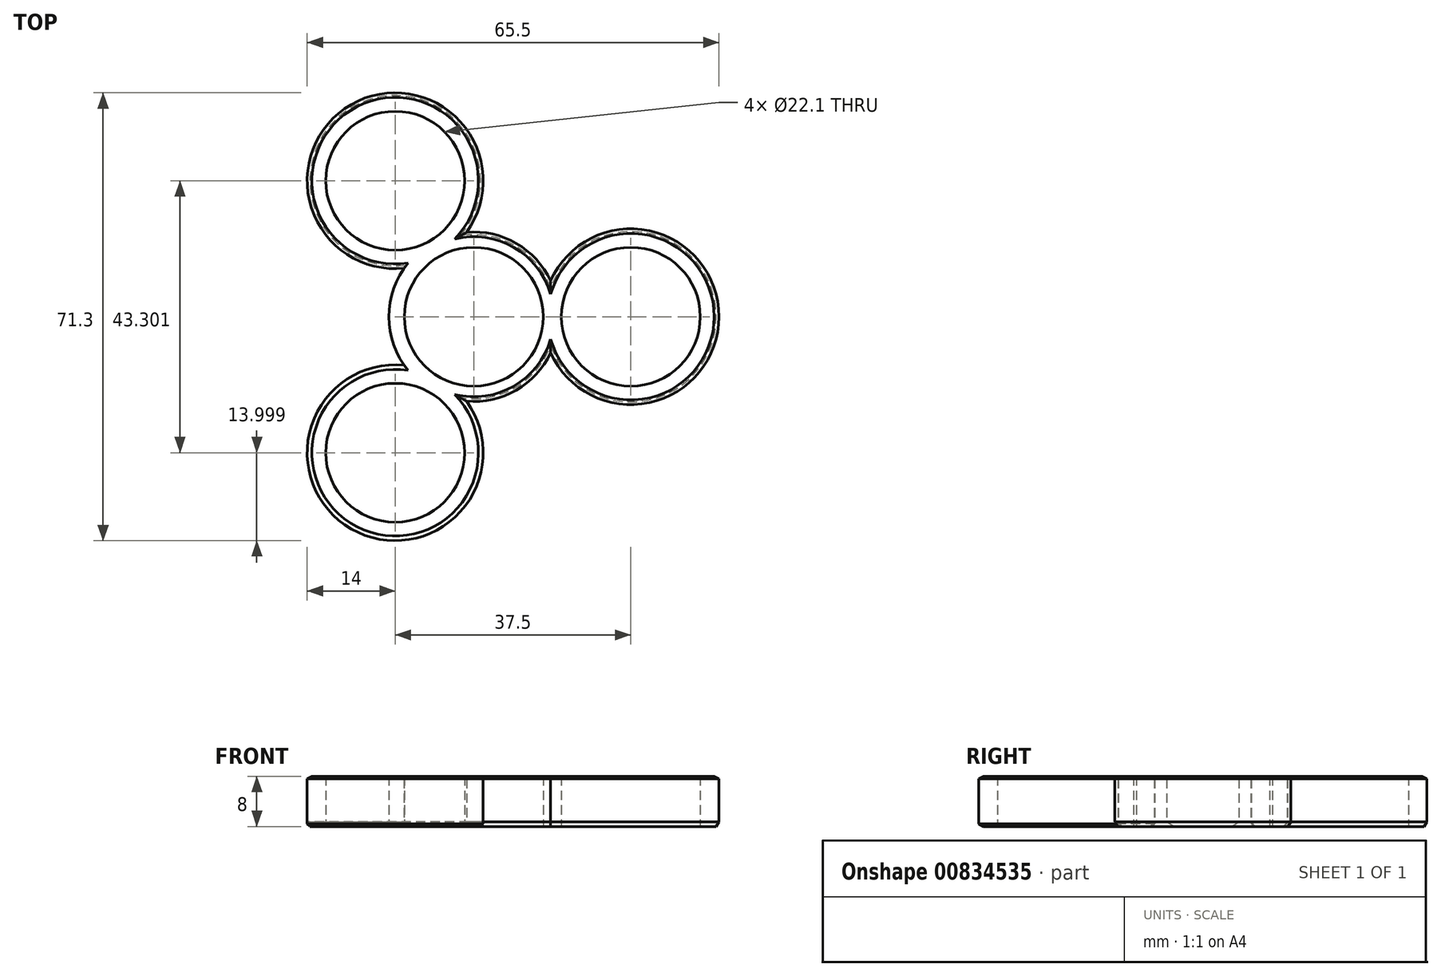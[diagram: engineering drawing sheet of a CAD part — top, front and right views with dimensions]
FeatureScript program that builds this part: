
annotation { "Feature Type Name" : "Feature", "Feature Type Description" : "" }
export const myFeature = defineFeature(function(context is Context, id is Id, definition is map)
    precondition{}
    {
        {
            var Q0;
            Q0=qCreatedBy(makeId("Top.planeOp"),FACE);
            var sketch = newSketch(context, id + "F0", { "sketchPlane" : qUnion([Q0])});
            skCircle(sketch, "E0", {"center": v(0, 0) * mm, "radius": 11.05 * mm});
            skCircle(sketch, "E1", {"center": v(25, 0) * mm, "radius": 11.05 * mm});
            skCircle(sketch, "E2.1.0", {"center": v(-12.5, 21.65) * mm, "radius": 11.05 * mm});
            skCircle(sketch, "E2.2.0", {"center": v(-12.5, -21.65) * mm, "radius": 11.05 * mm});
            skSolve(sketch);
        }
        {
            var Q0;
            Q0=qCreatedBy(makeId("Top.planeOp"),FACE);
            var sketch = newSketch(context, id + "F1", { "sketchPlane" : qUnion([Q0])});
            skPoint(sketch, "E3.0", {"position": v(-12.5, 21.65) * mm});
            skCircle(sketch, "E4.0.0", {"center": v(-12.5, 21.65) * mm, "radius": 11.05 * mm});
            skCircle(sketch, "E5.0.0", {"center": v(25, 0) * mm, "radius": 11.05 * mm});
            skCircle(sketch, "E6.0.0", {"center": v(-12.5, -21.65) * mm, "radius": 11.05 * mm});
            skCircle(sketch, "E7.0.0", {"center": v(0, 0) * mm, "radius": 11.05 * mm});
            skCircle(sketch, "E8", {"center": v(25, 0) * mm, "radius": 14 * mm});
            skCircle(sketch, "E9", {"center": v(-12.5, 21.65) * mm, "radius": 14 * mm});
            skCircle(sketch, "E10", {"center": v(-12.5, -21.65) * mm, "radius": 14 * mm});
            skCircle(sketch, "E11", {"center": v(0, 0) * mm, "radius": 13.5 * mm});
            skSolve(sketch);
        }
        {
            var Q0;
            Q0=makeQuery(id+"F1.imprint","IMPRINT",FACE,{"disambiguationData":[TD([[makeQuery(id+"F1.imprint","IMPRINT",EDGE,{"derivedFrom":sQuery(id+"F1.wireOp",EDGE,"E4.0.0")}),-1.0]])]});
            var Q1;
            Q1=makeQuery(id+"F1.imprint","IMPRINT",FACE,{"disambiguationData":[TD([[makeQuery(id+"F1.imprint","IMPRINT",EDGE,{"derivedFrom":sQuery(id+"F1.wireOp",EDGE,"E7.0.0")}),-1.0]])]});
            var Q2;
            {var subQ0=sQuery(id+"F1.wireOp",EDGE,"E11");var subQ1=sQuery(id+"F1.wireOp",EDGE,"E9");var subQ2=makeQuery(id+"F1.imprint","INTERSECT",VERTEX,{"disambiguationData":[OD(0.0)],"derivedFrom":[subQ1,subQ0]});Q2=makeQuery(id+"F1.imprint","IMPRINT",FACE,{"disambiguationData":[TD([[makeQuery(id+"F1.imprint","IMPRINT",EDGE,{"disambiguationData":[TD([[subQ2,1.0]])],"derivedFrom":subQ1}),1.0]])]});}
            var Q3;
            {var subQ0=sQuery(id+"F1.wireOp",EDGE,"E11");var subQ1=sQuery(id+"F1.wireOp",EDGE,"E8");var subQ2=makeQuery(id+"F1.imprint","INTERSECT",VERTEX,{"disambiguationData":[OD(0.0)],"derivedFrom":[subQ1,subQ0]});Q3=makeQuery(id+"F1.imprint","IMPRINT",FACE,{"disambiguationData":[TD([[makeQuery(id+"F1.imprint","IMPRINT",EDGE,{"disambiguationData":[TD([[subQ2,-1.0]])],"derivedFrom":subQ1}),1.0]])]});}
            var Q4;
            Q4=makeQuery(id+"F1.imprint","IMPRINT",FACE,{"disambiguationData":[TD([[makeQuery(id+"F1.imprint","IMPRINT",EDGE,{"derivedFrom":sQuery(id+"F1.wireOp",EDGE,"E5.0.0")}),-1.0]])]});
            var Q5;
            {var subQ0=sQuery(id+"F1.wireOp",EDGE,"E11");var subQ1=sQuery(id+"F1.wireOp",EDGE,"E10");var subQ2=makeQuery(id+"F1.imprint","INTERSECT",VERTEX,{"disambiguationData":[OD(0.0)],"derivedFrom":[subQ1,subQ0]});Q5=makeQuery(id+"F1.imprint","IMPRINT",FACE,{"disambiguationData":[TD([[makeQuery(id+"F1.imprint","IMPRINT",EDGE,{"disambiguationData":[TD([[subQ2,1.0]])],"derivedFrom":subQ1}),1.0]])]});}
            var Q6;
            Q6=makeQuery(id+"F1.imprint","IMPRINT",FACE,{"disambiguationData":[TD([[makeQuery(id+"F1.imprint","IMPRINT",EDGE,{"derivedFrom":sQuery(id+"F1.wireOp",EDGE,"E6.0.0")}),-1.0]])]});
            extrude(context, id + "F2", {"entities" : qUnion([Q0, Q1, Q2, Q3, Q4, Q5, Q6]), "depth" : 8 * mm, "offsetDistance" : 25 * mm});
        }
        {
            var Q0;
            Q0=makeQuery(id+"F2.opExtrude","CAP_EDGE",EDGE,{"disambiguationData":[OSD([sQuery(id+"F1.wireOp",EDGE,"E10")])],"isStart":false});
            var Q1;
            {var subQ0=sQuery(id+"F1.wireOp",EDGE,"E11");Q1=makeQuery(id+"F2.opExtrude","CAP_EDGE",EDGE,{"disambiguationData":[OSD([subQ0]),TDD([makeQuery(id+"F1.imprint","IMPRINT",EDGE,{"disambiguationData":[TD([[makeQuery(id+"F1.imprint","INTERSECT",VERTEX,{"disambiguationData":[OD(1.0)],"derivedFrom":[sQuery(id+"F1.wireOp",EDGE,"E8"),subQ0]}),1.0]])],"derivedFrom":subQ0})])],"isStart":false});}
            var Q2;
            Q2=makeQuery(id+"F2.opExtrude","CAP_EDGE",EDGE,{"disambiguationData":[OSD([sQuery(id+"F1.wireOp",EDGE,"E8")])],"isStart":false});
            var Q3;
            {var subQ0=sQuery(id+"F1.wireOp",EDGE,"E11");Q3=makeQuery(id+"F2.opExtrude","CAP_EDGE",EDGE,{"disambiguationData":[OSD([subQ0]),TDD([makeQuery(id+"F1.imprint","IMPRINT",EDGE,{"disambiguationData":[TD([[makeQuery(id+"F1.imprint","INTERSECT",VERTEX,{"disambiguationData":[OD(0.0)],"derivedFrom":[sQuery(id+"F1.wireOp",EDGE,"E8"),subQ0]}),-1.0]])],"derivedFrom":subQ0})])],"isStart":false});}
            var Q4;
            {var subQ0=sQuery(id+"F1.wireOp",EDGE,"E11");Q4=makeQuery(id+"F2.opExtrude","CAP_EDGE",EDGE,{"disambiguationData":[OSD([subQ0]),TDD([makeQuery(id+"F1.imprint","IMPRINT",EDGE,{"disambiguationData":[TD([[makeQuery(id+"F1.imprint","INTERSECT",VERTEX,{"disambiguationData":[OD(1.0)],"derivedFrom":[sQuery(id+"F1.wireOp",EDGE,"E9"),subQ0]}),-1.0]])],"derivedFrom":subQ0})])],"isStart":false});}
            var Q5;
            Q5=makeQuery(id+"F2.opExtrude","CAP_EDGE",EDGE,{"disambiguationData":[OSD([sQuery(id+"F1.wireOp",EDGE,"E9")])],"isStart":false});
            var Q6;
            Q6=makeQuery(id+"F2.opExtrude","CAP_EDGE",EDGE,{"disambiguationData":[OSD([sQuery(id+"F1.wireOp",EDGE,"E10")])],"isStart":true});
            var Q7;
            {var subQ0=sQuery(id+"F1.wireOp",EDGE,"E11");Q7=makeQuery(id+"F2.opExtrude","CAP_EDGE",EDGE,{"disambiguationData":[OSD([subQ0]),TDD([makeQuery(id+"F1.imprint","IMPRINT",EDGE,{"disambiguationData":[TD([[makeQuery(id+"F1.imprint","INTERSECT",VERTEX,{"disambiguationData":[OD(1.0)],"derivedFrom":[sQuery(id+"F1.wireOp",EDGE,"E8"),subQ0]}),1.0]])],"derivedFrom":subQ0})])],"isStart":true});}
            var Q8;
            Q8=makeQuery(id+"F2.opExtrude","CAP_EDGE",EDGE,{"disambiguationData":[OSD([sQuery(id+"F1.wireOp",EDGE,"E8")])],"isStart":true});
            var Q9;
            {var subQ0=sQuery(id+"F1.wireOp",EDGE,"E11");Q9=makeQuery(id+"F2.opExtrude","CAP_EDGE",EDGE,{"disambiguationData":[OSD([subQ0]),TDD([makeQuery(id+"F1.imprint","IMPRINT",EDGE,{"disambiguationData":[TD([[makeQuery(id+"F1.imprint","INTERSECT",VERTEX,{"disambiguationData":[OD(1.0)],"derivedFrom":[sQuery(id+"F1.wireOp",EDGE,"E9"),subQ0]}),-1.0]])],"derivedFrom":subQ0})])],"isStart":true});}
            var Q10;
            {var subQ0=sQuery(id+"F1.wireOp",EDGE,"E11");Q10=makeQuery(id+"F2.opExtrude","CAP_EDGE",EDGE,{"disambiguationData":[OSD([subQ0]),TDD([makeQuery(id+"F1.imprint","IMPRINT",EDGE,{"disambiguationData":[TD([[makeQuery(id+"F1.imprint","INTERSECT",VERTEX,{"disambiguationData":[OD(0.0)],"derivedFrom":[sQuery(id+"F1.wireOp",EDGE,"E8"),subQ0]}),-1.0]])],"derivedFrom":subQ0})])],"isStart":true});}
            var Q11;
            Q11=makeQuery(id+"F2.opExtrude","CAP_EDGE",EDGE,{"disambiguationData":[OSD([sQuery(id+"F1.wireOp",EDGE,"E9")])],"isStart":true});
            chamfer(context, id + "F3", {"entities" : qUnion([Q0, Q1, Q2, Q3, Q4, Q5, Q6, Q7, Q8, Q9, Q10, Q11]), "chamferType" : ChamferType.OFFSET_ANGLE, "width" : 0.75 * mm, "oppositeDirection" : false, "angle" : 30 * degree, "tangentPropagation" : true});
        }
    });
